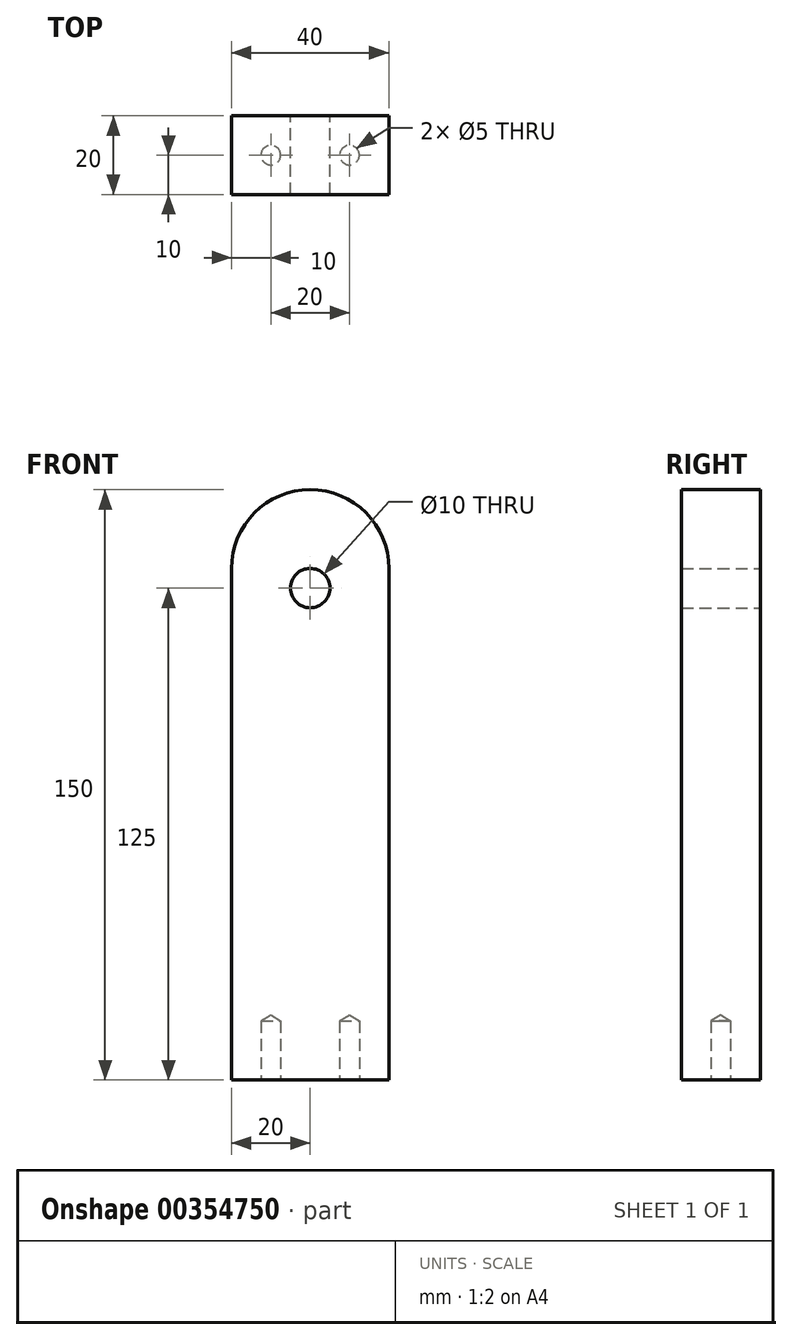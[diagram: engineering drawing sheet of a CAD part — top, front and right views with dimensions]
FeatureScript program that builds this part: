
annotation { "Feature Type Name" : "Feature", "Feature Type Description" : "" }
export const myFeature = defineFeature(function(context is Context, id is Id, definition is map)
    precondition{}
    {
        {
            var Q0;
            Q0=qCreatedBy(makeId("Front.planeOp"),FACE);
            var sketch = newSketch(context, id + "F0", { "sketchPlane" : qUnion([Q0])});
            skLineSegment(sketch, "E0.bottom", {"start": v(0, 75) * mm, "end": v(0, 75) * mm});
            skLineSegment(sketch, "E0.top", {"start": v(20, -75) * mm, "end": v(-20, -75) * mm});
            skLineSegment(sketch, "E0.left", {"start": v(20, 55) * mm, "end": v(20, -75) * mm});
            skLineSegment(sketch, "E0.right", {"start": v(-20, 55) * mm, "end": v(-20, -75) * mm});
            skPoint(sketch, "E0.middle", {"position": v(0, 0) * mm});
            skPoint(sketch, "E1.endSnap0", {"position": v(0, -75) * mm});
            skCircle(sketch, "E2", {"center": v(0, 50) * mm, "radius": 5 * mm});
            skPoint(sketch, "E3.visualSharp", {"position": v(-20, 75) * mm});
            skArc(sketch, "E3.filletArc", {"start": v(0, 75) * mm, "mid": v(-14.14, 69.14) * mm, "end": v(-20, 55) * mm});
            skPoint(sketch, "E4.visualSharp", {"position": v(20, 75) * mm});
            skArc(sketch, "E4.filletArc", {"start": v(20, 55) * mm, "mid": v(14.14, 69.14) * mm, "end": v(0, 75) * mm});
            skSolve(sketch);
        }
        {
            var Q0;
            Q0 = qSketchRegion(id + "F0", true);
            extrude(context, id + "F1", {"entities" : qUnion([Q0]), "depth" : 20 * mm});
        }
        {
            var Q0;
            Q0=makeQuery(id+"F1.opExtrude","SWEPT_FACE",FACE,{"disambiguationData":[OSD([sQuery(id+"F0.wireOp",EDGE,"E0.top")])]});
            var sketch = newSketch(context, id + "F2", { "sketchPlane" : qUnion([Q0])});
            skPoint(sketch, "E5.endSnap0", {"position": v(20, 10) * mm});
            skCircle(sketch, "E6", {"center": v(-10, 10) * mm, "radius": 2 * mm});
            skCircle(sketch, "E7", {"center": v(10, 10) * mm, "radius": 2 * mm});
            skSolve(sketch);
        }
        {
            var Q0;
            Q0=sQuery(id+"F2.wireOp",VERTEX,"E6.center");
            var Q1;
            Q1=sQuery(id+"F2.wireOp",VERTEX,"E7.center");
            var Q2;
            Q2=makeQuery(id+"F1.opExtrude","SWEPT_BODY",BODY,{"disambiguationData":[OSD([sQuery(id+"F0.wireOp",EDGE,"E0.top"),sQuery(id+"F0.wireOp",EDGE,"E0.left"),sQuery(id+"F0.wireOp",EDGE,"E0.right"),sQuery(id+"F0.wireOp",EDGE,"E2"),sQuery(id+"F0.wireOp",EDGE,"E3.filletArc"),sQuery(id+"F0.wireOp",EDGE,"E4.filletArc")])]});
            hole(context, id + "F3", {"style" : HoleStyle.SIMPLE, "endStyle" : HoleEndStyle.BLIND, "standardTappedOrClearance" : lookupTablePath({ "standard" : "ISO", "engagement" : "75%", "pitch" : "1 mm", "size" : "M6", "type" : "Tapped" }), "standardBlindInLast" : lookupTablePath({ "standard" : "ISO", "engagement" : "75%", "pitch" : "1 mm", "size" : "M6", "type" : "Tapped" }), "holeDiameter" : 5 * mm, "showTappedDepth" : true, "holeDepth" : 15 * mm, "isTappedThrough" : true, "tappedDepth" : 12 * mm, "tapClearance" : 3, "startFromSketch" : true, "locations" : qUnion([Q0, Q1]), "scope" : qUnion([Q2]), "majorDiameter" : 6 * mm});
        }
    });
